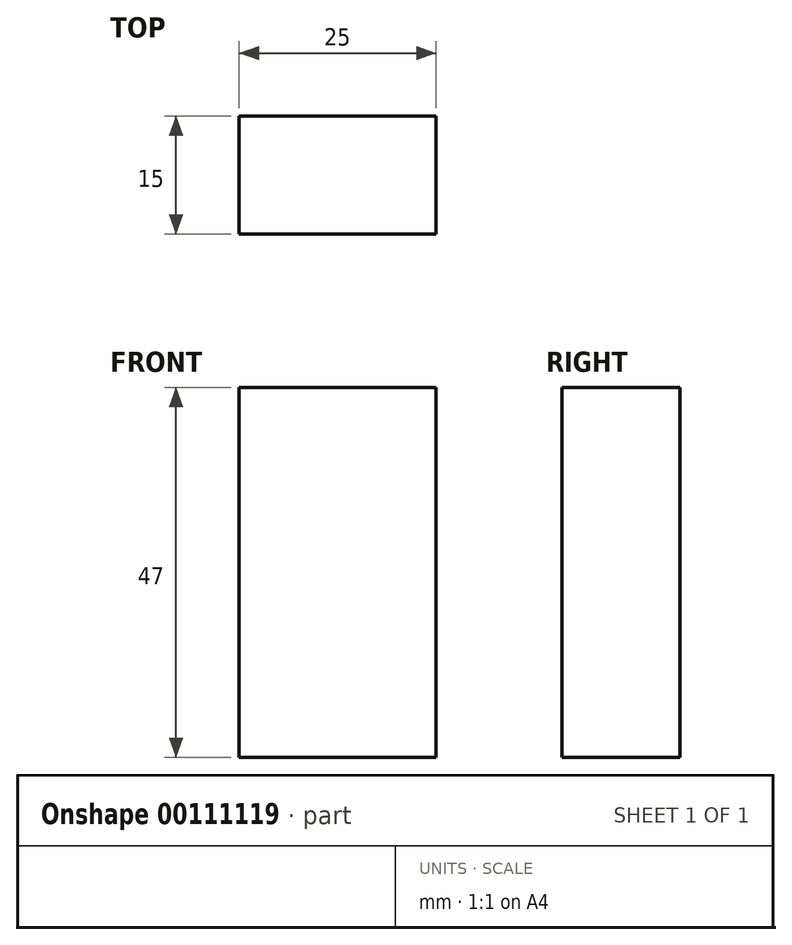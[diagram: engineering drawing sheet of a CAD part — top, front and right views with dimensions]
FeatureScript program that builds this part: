
annotation { "Feature Type Name" : "Feature", "Feature Type Description" : "" }
export const myFeature = defineFeature(function(context is Context, id is Id, definition is map)
    precondition{}
    {
        {
            var Q0;
            Q0=qCreatedBy(makeId("Front.planeOp"),FACE);
            var sketch = newSketch(context, id + "F0", { "sketchPlane" : qUnion([Q0])});
            skLineSegment(sketch, "E0.bottom", {"start": v(12.5, -23.5) * mm, "end": v(-12.5, -23.5) * mm});
            skLineSegment(sketch, "E0.top", {"start": v(12.5, 23.5) * mm, "end": v(-12.5, 23.5) * mm});
            skLineSegment(sketch, "E0.left", {"start": v(12.5, -23.5) * mm, "end": v(12.5, 23.5) * mm});
            skLineSegment(sketch, "E0.right", {"start": v(-12.5, -23.5) * mm, "end": v(-12.5, 23.5) * mm});
            skPoint(sketch, "E0.middle", {"position": v(0, 0) * mm});
            skSolve(sketch);
        }
        {
            var Q0;
            Q0 = qSketchRegion(id + "F0", true);
            extrude(context, id + "F1", {"entities" : qUnion([Q0]), "depth" : 15 * mm});
        }
    });
